# Revit family: IS_ConnectSpace_E0396_BIM_DE
name_source: partatom
category: Plumbing Fixtures
revit_build: Autodesk Revit MEP 2016 (Build: 20161004_0715(x64)
units: mm (PartAtom-declared; Revit-internal decimal feet)

## family parameters
Always vertical = No
Cut with Voids When Loaded = No
OmniClass Number = 23.45.05.17
OmniClass Title = Sanitary Leisure Units
Part Type = Normal
Room Calculation Point = No
Round Connector Dimension = Use Diameter
Shared = No
Work Plane-Based = No

## types (1)
- E039667 - CONNECT SPACE box for vanity unit 157x112mm
    Accessories = www.idealstandard.de\ersatzteile
    AssetType = Fixed
    BIMObjectName = ISI_IdealStandard_VanityUnits_ConnectSpace_E039667
    BIMobject category = Storage
    BOSUseNativeGeometries = 1
    BarCode = 5017830455677
    Brand = Ideal Standard
    Brand url = http://www.idealstandard.de
    CodePerformance = 0
    Color = NEUTRAL
    ConnectionType = Plumbing
    Cost = 0 $
    CurrencyUnit = €
    CurrentRevision = 1
    Date of publishing = 20/12/2017
    Description = IS Aufbewahrungsbox CONNECT SPACE, 157x112x72mm, hellgrau
    DurationUnit = Year
    EAN code = https://5017830455677
    Edition number = 1
    ExpectedLife = 25
    Features = IS Aufbewahrungsbox CONNECT SPACE, 157x112x72mm, hellgrau
    Finish = NEUTRAL
    IFC Classification = Sanitary Terminal
    IfcExportAs = IfcSanitaryTerminalType
    Installation instructions = http://www.idealstandard.de
    InstallationInstructions = www.idealstandard.de\produkte
    MainColor = NEUTRAL
    MaintenanceInformation = www.idealstandard.de\produkte
    Manufacturer name = Ideal Standard
    ManufacturerURL = http://www.idealstandard.de
    Material = 0
    Model = E039667
    ModelNumber = E039667
    ModelReference = IS Aufbewahrungsbox CONNECT SPACE, 157x112x72mm, hellgrau
    NBS Reference Code = 35-75-94
    NBS Reference Description = Vanity Units
    Name = VanityUnits_ConnectSpace_E039667
    NettWeight = 0.15 Kg
    Nominal height = 72
    Nominal width = 157
    NominalDepth = 114 mm  [stored 0.374016 ft]
    NominalHeight = 77 mm
    NominalLength = 114 mm  [stored 0.374016 ft]
    NominalWidth = 159 mm
    Product Guid = aad79185-2b79-4c08-a629-ebfb742c2571
    Product SKU = E0396
    Product data url = https://bimobject.com
    Product family = Sanitary
    Product group = Furniture
    Product name = CONNECT SPACE box for vanity unit 157x112mm
    Product url = http://www.idealstandard.de
    ProductInformation = www.idealstandard.de/produkte
    QR code = http://bimobject.com
    Shape = Sculptured
    Size = 77 x 114 x 159mm
    Space = Internal
    SpareParts = www.idealstandard.de/ersatzteile
    Technical description = http://www.idealstandard.de
    URL = http://www.idealstandard.de
    Uniclass 2.0 Code = PR-35-75-94
    Uniclass 2.0 Description = Vanity Units
    Uniclass 2015 Code = Pr_40_20_76_94
    Uniclass 2015 Name = Vanity units
    Uniclass2015Code = Pr_40_20_76_94
    Uniclass2015Title = Vanity units
    Uniclass2015Version = Products v1.1
    Version = 1
    VolumeUnits = Litres
    Weight Net (Kg) = 0.15

note: [stored X ft] marks values corroborated as IEEE doubles in the binary element streams (Revit-internal decimal feet)

## geometry (parser evidence)
native form markers: Blend x4
no freeform markers — native parametric forms only
